# Revit family: HERZ Diaphragm Pressure Reducing Valve With Plastic Cap 2682
name_source: partatom
category: Rohrzubehör
units: mm (PartAtom-declared; Revit-internal decimal feet)

## family parameters
Arbeitsebenenbasiert = Nein
Beim Laden mit Abzugskörper schneiden = Nein
Bemaßung runder Anschluss = Durchmesser verwenden
Gemeinsam genutzt = Nein
Immer vertikal = Ja
OmniClass-Nummer = 23.65.55.14
OmniClass-Titel = Valves for Liquid Services
Teiletyp = Unterbricht

## types (2) — shared parameters
B02 = 26 mm  [stored 0.0853018 ft]
B03 = 5 mm  [stored 0.0164042 ft]
Body = forged brass acc. to EN 12165; CW626N
Bottom cover = PA12, transparent
Diaphragm = EPDM
External thread = acc. to ISO 7-1 and ISO228
Factory settings = 300000.0 Pa
Filter = stainless stee, mesh size 0.3 mm
Handle = PA 6.6, green
Hersteller = HERZ Armaturen Ges.m.b.H.
Manometer scale = 0 - 10 bar
Max. inlet pressure = 1600000.0 Pa
Max. operating temperature = 40 °C
Medium = water
Outlet pressure range = 1.5 - 6 bar
Pressure gauge connectors = 1/4" F (ISO 228-1)
R06 = 19.5 mm  [stored 0.0639764 ft]
S02 = 10 mm  [stored 0.0328084 ft]
SCTWCODE = 04;24;02
SCTWSEQ = AW;SBT_TYP_AW="111";2
Sealing = EPDM
Spring = spring steel
Spring guide = stainless steel
Standard = EN 1567
Upper part = PA6.6
W01 = 91.00°
zero-valued in all types: SC_NennweiteBerechnet, Vorgabe-Ansicht

## per-type parameters (varying)
| type | Application | Note | URL |
| Manometer front | Typischerweise dient der Druckreduzierer dazu, Installationen beziehungsweise Anlagen vor zu hohem Druck zu schützen.
Weiters können Druckreduzierer in Heizungsanlagen eingesetzt werden, um zu hohe Drücke im Boiler zu verhindern.
Der Druck nach dem Druckreduzierer ist im angegebenen Bereich einstellbar und steht nicht im Zusammenhang mit dem Vordruck.
Um den Druck nach dem Druckreduzierer zu steigern, muss der Handgriff im Uhrzeigersinn gedreht werden.
Durch das Einstellen von Drücken, welche die vorgegebene Skala überschreiten, können Schäden am Druckreduzierer entstehen.
Wir empfehlen einen maximalen Hinterdruck sekundärseitig von 4 bar für Anlagen in privaten Haushalten (lange Produktlebensdauer, geringe Kosten).
Nach jeder Änderung des Einstellwertes muss die Ausgangsseite druckentlastet werden, zum Beispiel durch Wasserzapfen. | Gemäß Art 33 der REACH-Verordnung (EG Nr. 1907/2006) sind wir verpflichtet, darauf hinzuweisen, dass der Stoff Blei auf der SVHC-Liste geführt wird und dass alle aus Messing bestehenden Bauteile, die in unseren Erzeugnissen verarbeitet sind, mehr als 0,1 % (w/w) Blei (CAS: 7439-92-1 / EINECS: 231-100-4) enthalten.
Da Blei als Legierungsbestandteil fest gebunden ist, sind keine Expositionen zu erwarten und daher sind keine zusätzlichen Angaben zur sicheren Verwendung notwendig. | www.herz-armaturen.at |
| Manometer back | The pressure reducing valve protects installations against over pressure (reduces input pressure to a working level).
It can also be used in heating systems to protect boiler against increased pressure.
The outlet pressure is adjustable and does not vary with changes of the inlet pressure.
The outlet pressure can be adjusted by turning the green handle.
Turning the handle clockwise increases the outlet pressure.
Turning above the stated values on the pressure reducer scale may damage the valve.
We recommend the max. outlet pressure of 4 bar for private house installations (product long life, costs,...).
After each new setting of the outlet pressure, the regulated pipe has to be opened and closed. | Pursuant to Article 33 of the REACH Regulation (EC No. 1907/2006), we are obliged to point out that the material lead is listed on the SVHC list and that all brass components manufactured in our products exceed 0.1% (w / w) lead (CAS: 7439-92-1 / EINECS: 231-100-4).
Since lead is a component part of an alloy, actual exposure is not possible and therefore no additional information on safe use is necessary. | www.herzvalves.com |

note: [stored X ft] marks values corroborated as IEEE doubles in the binary element streams (Revit-internal decimal feet)

## geometry (parser evidence)
native form markers: Extrusion x1
no freeform markers — native parametric forms only
